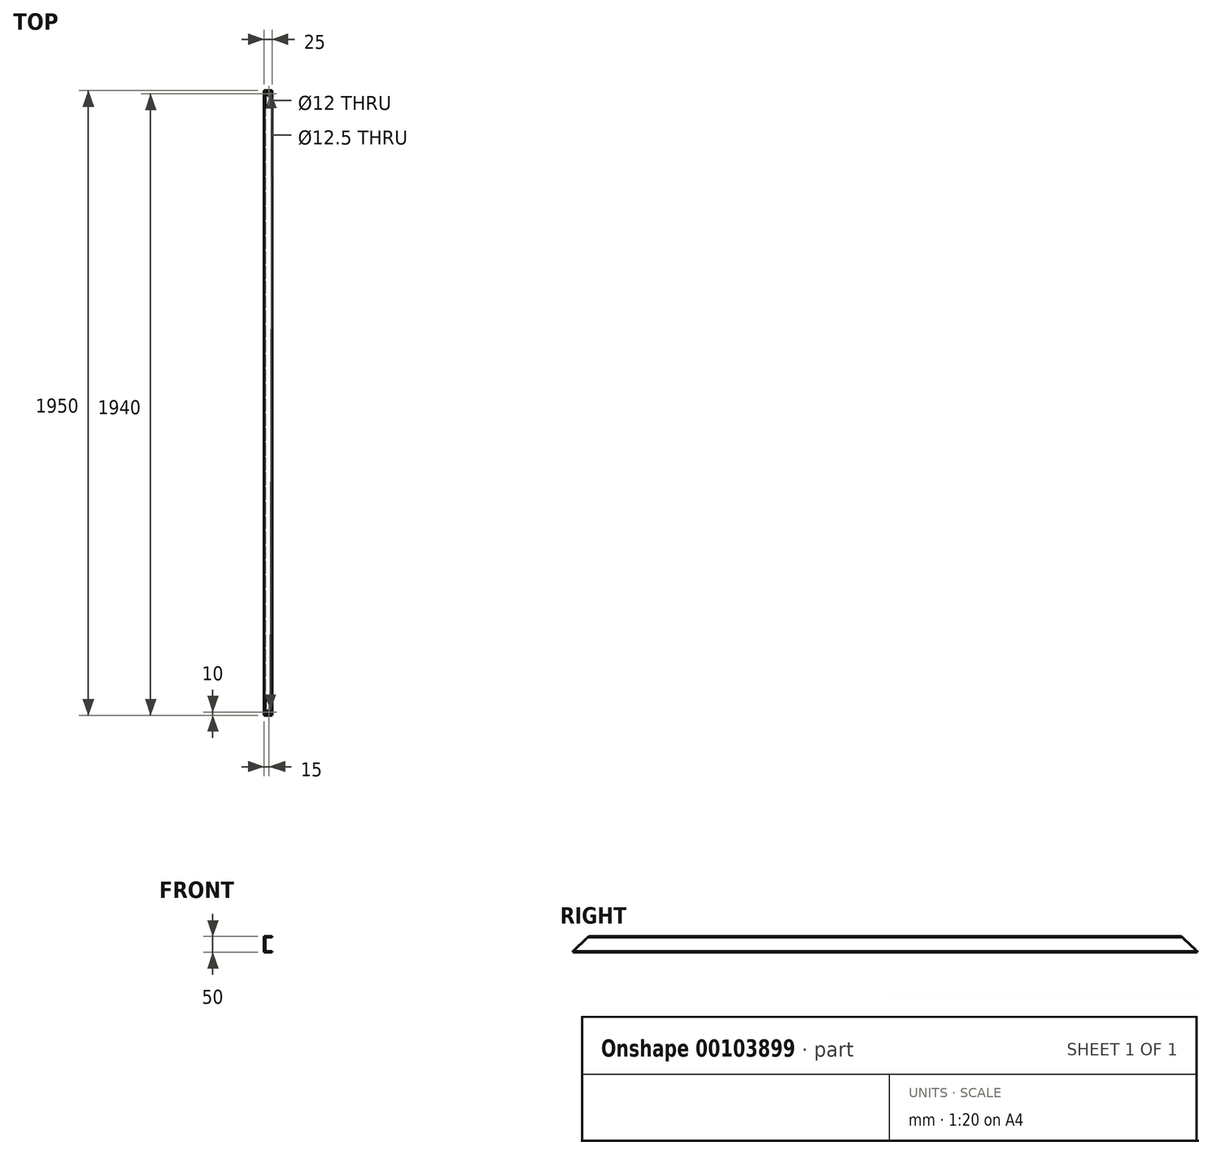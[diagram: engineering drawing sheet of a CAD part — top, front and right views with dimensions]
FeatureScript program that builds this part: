
annotation { "Feature Type Name" : "Feature", "Feature Type Description" : "" }
export const myFeature = defineFeature(function(context is Context, id is Id, definition is map)
    precondition{}
    {
        {
            var Q0;
            Q0=qCreatedBy(makeId("Front.planeOp"),FACE);
            var sketch = newSketch(context, id + "F0", { "sketchPlane" : qUnion([Q0])});
            skLineSegment(sketch, "E0.bottom", {"start": v(25, 0) * mm, "end": v(0, 0) * mm});
            skLineSegment(sketch, "E0.top", {"start": v(25, 50) * mm, "end": v(0, 50) * mm});
            skLineSegment(sketch, "E0.left", {"start": v(25, 0) * mm, "end": v(25, 3) * mm});
            skLineSegment(sketch, "E0.right", {"start": v(0, 0) * mm, "end": v(0, 50) * mm});
            skLineSegment(sketch, "E1.0", {"start": v(25, 47) * mm, "end": v(8, 47) * mm});
            skLineSegment(sketch, "E1.1", {"start": v(3, 8) * mm, "end": v(3, 42) * mm});
            skLineSegment(sketch, "E1.2", {"start": v(25, 3) * mm, "end": v(8, 3) * mm});
            skLineSegment(sketch, "E2.trimOffspring", {"start": v(25, 47) * mm, "end": v(25, 50) * mm});
            skPoint(sketch, "E3.visualSharp", {"position": v(3, 47) * mm});
            skArc(sketch, "E3.filletArc", {"start": v(8, 47) * mm, "mid": v(4.46, 45.54) * mm, "end": v(3, 42) * mm});
            skPoint(sketch, "E4.visualSharp", {"position": v(3, 3) * mm});
            skArc(sketch, "E4.filletArc", {"start": v(3, 8) * mm, "mid": v(4.46, 4.46) * mm, "end": v(8, 3) * mm});
            skPoint(sketch, "E5.visualSharp", {"position": v(0, 50) * mm});
            skLineSegment(sketch, "E5.filletArc", {"start": v(0, 50) * mm, "end": v(0, 50) * mm});
            skPoint(sketch, "E6.visualSharp", {"position": v(25, 50) * mm});
            skLineSegment(sketch, "E6.filletArc", {"start": v(25, 50) * mm, "end": v(25, 50) * mm});
            skPoint(sketch, "E7.visualSharp", {"position": v(25, 47) * mm});
            skLineSegment(sketch, "E7.filletArc", {"start": v(25, 47) * mm, "end": v(25, 47) * mm});
            skPoint(sketch, "E8.visualSharp", {"position": v(0, 0) * mm});
            skLineSegment(sketch, "E8.filletArc", {"start": v(0, 0) * mm, "end": v(0, 0) * mm});
            skPoint(sketch, "E9.visualSharp", {"position": v(25, 0) * mm});
            skLineSegment(sketch, "E9.filletArc", {"start": v(25, 0) * mm, "end": v(25, 0) * mm});
            skPoint(sketch, "E10.visualSharp", {"position": v(25, 3) * mm});
            skLineSegment(sketch, "E10.filletArc", {"start": v(25, 3) * mm, "end": v(25, 3) * mm});
            skSolve(sketch);
        }
        {
            var Q0;
            Q0 = qSketchRegion(id + "F0", true);
            extrude(context, id + "F1", {"entities" : qUnion([Q0]), "oppositeDirection" : true, "depth" : 1950 * mm});
        }
        {
            var Q0;
            Q0=qCreatedBy(makeId("Right.planeOp"),FACE);
            var sketch = newSketch(context, id + "F2", { "sketchPlane" : qUnion([Q0])});
            skLineSegment(sketch, "E11.0", {"start": v(0, 3) * mm, "end": v(0, 50) * mm});
            skLineSegment(sketch, "E12.0", {"start": v(0, 50) * mm, "end": v(50, 50) * mm});
            skLineSegment(sketch, "E13.0", {"start": v(0, 49) * mm, "end": v(0, 50) * mm});
            skLineSegment(sketch, "E14.0.0", {"start": v(0, 0) * mm, "end": v(0, 3) * mm});
            skLineSegment(sketch, "E14.0.2", {"start": v(1950, 0) * mm, "end": v(1950, 0) * mm});
            skPoint(sketch, "E15.orphan", {"position": v(0, 0) * mm});
            skLineSegment(sketch, "E16", {"start": v(50, 50) * mm, "end": v(0, 3) * mm});
            skPoint(sketch, "E17.orphan", {"position": v(1950, 50) * mm});
            skPoint(sketch, "E18.0.start.orphan", {"position": v(1950, 3) * mm});
            skSolve(sketch);
        }
        {
            var Q0;
            Q0 = qSketchRegion(id + "F2", true);
            extrude(context, id + "F3", {"entities" : qUnion([Q0]), "operationType" : NewBodyOperationType.REMOVE, "depth" : 25 * mm});
        }
        {
            var Q0;
            Q0=makeQuery(id+"F1.opExtrude","SWEPT_FACE",FACE,{"disambiguationData":[OSD([sQuery(id+"F0.wireOp",EDGE,"E0.right")])]});
            var sketch = newSketch(context, id + "F4", { "sketchPlane" : qUnion([Q0])});
            skLineSegment(sketch, "E19.0", {"start": v(-1900, 50) * mm, "end": v(-1950, 50) * mm});
            skLineSegment(sketch, "E20.0", {"start": v(-1950, 0) * mm, "end": v(-1950, 3) * mm});
            skLineSegment(sketch, "E21.0", {"start": v(-1950, 50) * mm, "end": v(-1950, 0) * mm});
            skPoint(sketch, "E22.orphan", {"position": v(-1950, 0) * mm});
            skLineSegment(sketch, "E23", {"start": v(-1900, 50) * mm, "end": v(-1950, 3) * mm});
            skPoint(sketch, "E24.orphan", {"position": v(-50, 50) * mm});
            skPoint(sketch, "E25.0.end.orphan", {"position": v(0, 3) * mm});
            skSolve(sketch);
        }
        {
            var Q0;
            Q0 = qSketchRegion(id + "F4", true);
            extrude(context, id + "F5", {"entities" : qUnion([Q0]), "operationType" : NewBodyOperationType.REMOVE, "oppositeDirection" : true, "depth" : 25 * mm});
        }
        {
            var Q0;
            Q0=makeQuery(id+"F1.opExtrude","SWEPT_FACE",FACE,{"disambiguationData":[OSD([sQuery(id+"F0.wireOp",EDGE,"E1.2")])]});
            var sketch = newSketch(context, id + "F6", { "sketchPlane" : qUnion([Q0])});
            skCircle(sketch, "E26", {"center": v(15, 10) * mm, "radius": 6 * mm});
            skSolve(sketch);
        }
        {
            var Q0;
            Q0 = qSketchRegion(id + "F6", true);
            extrude(context, id + "F7", {"entities" : qUnion([Q0]), "operationType" : NewBodyOperationType.REMOVE, "endBound" : BoundingType.THROUGH_ALL, "oppositeDirection" : true, "depth" : 25 * mm});
        }
        {
            var Q0;
            Q0=makeQuery(id+"F6.imprint","IMPRINT",FACE,{"disambiguationData":[TD([[makeQuery(id+"F6.imprint","IMPRINT",EDGE,{"derivedFrom":sQuery(id+"F6.wireOp",EDGE,"E26")}),-1.0]])]});
            var sketch = newSketch(context, id + "F8", { "sketchPlane" : qUnion([Q0])});
            skCircle(sketch, "E27", {"center": v(15, 1940) * mm, "radius": 6.25 * mm});
            skSolve(sketch);
        }
        {
            var Q0;
            Q0 = qSketchRegion(id + "F8", true);
            extrude(context, id + "F9", {"entities" : qUnion([Q0]), "operationType" : NewBodyOperationType.REMOVE, "endBound" : BoundingType.THROUGH_ALL, "oppositeDirection" : true, "depth" : 25 * mm});
        }
    });
